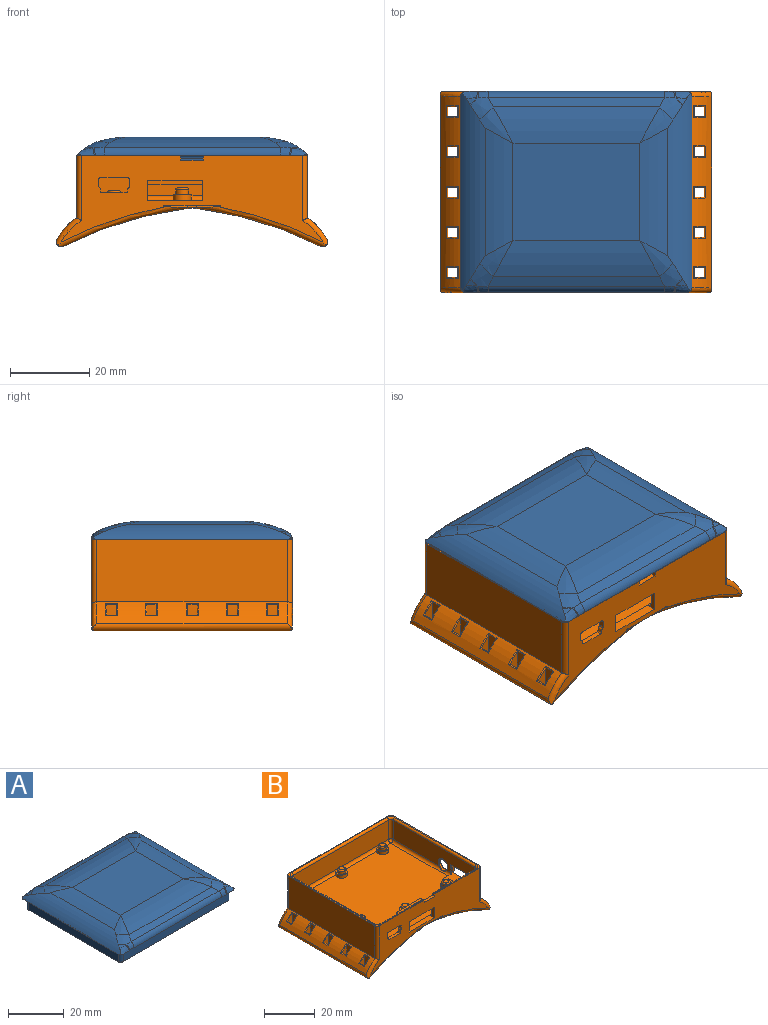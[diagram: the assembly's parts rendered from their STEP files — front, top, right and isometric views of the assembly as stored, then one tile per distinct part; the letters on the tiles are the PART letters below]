
ASSEMBLY  parts=2 mates=1
PART A: 92 faces, bbox 60.7x52.8x9.7 mm
  f0: plane 58.47x50.85mm, normal (0,0,-1), area 85.3mm2, adj f36,f37,f38,f39,f56,f57,f66,f67
  f1: cylinder r=1.27mm len=3.66mm, axis (0,0,1), area 7.3mm2, adj f5,f8,f59,f86
  f2: plane 0.08x0.07mm, normal (0,0,1), area 0mm2, adj f13,f80,f81
  f3: plane 0.08x0.07mm, normal (0,0,1), area 0mm2, adj f15,f80,f82
  f4: plane 0.08x0.07mm, normal (0,0,1), area 0mm2, adj f17,f82,f83
  f5: plane 45.72x3.66mm, normal (1,0,0), area 167.2mm2, adj f1,f9,f61,f84
  f6: plane 53.34x3.66mm, normal (0,1,0), area 195.1mm2, adj f9,f10,f65,f87
  f7: plane 45.72x3.66mm, normal (-1,0,0), area 167.2mm2, adj f10,f11,f62,f91
  f8: plane 53.34x3.66mm, normal (0,-1,0), area 195.1mm2, adj f1,f11,f58,f88
  f9: cylinder r=1.27mm len=3.66mm, axis (0,0,1), area 7.3mm2, adj f5,f6,f63,f85
  f10: cylinder r=1.27mm len=3.66mm, axis (0,0,1), area 7.3mm2, adj f6,f7,f64,f89
  f11: cylinder r=1.27mm len=3.66mm, axis (0,0,1), area 7.3mm2, adj f7,f8,f60,f90
  f12: plane 53.34x4.23mm, normal (0,-1,0), area 225.8mm2, adj f13,f19,f20,f81
  f13: cylinder r=0.64mm len=5.08mm, axis (0,0,1), area 4.7mm2, adj f2,f12,f14,f20,f80,f81
  f14: plane 45.72x4.21mm, normal (-1,0,0), area 192.3mm2, adj f13,f15,f20,f80
  f15: cylinder r=0.64mm len=5.08mm, axis (0,0,1), area 4.7mm2, adj f3,f14,f16,f20,f80,f82
  f16: plane 53.34x4.23mm, normal (0,1,0), area 225.8mm2, adj f15,f17,f20,f82
  f17: cylinder r=0.64mm len=5.08mm, axis (0,0,1), area 4.7mm2, adj f4,f16,f18,f20,f82,f83
  f18: plane 45.72x4.21mm, normal (1,0,0), area 192.3mm2, adj f17,f19,f20,f83
  f19: cylinder r=0.64mm len=5.08mm, axis (0,0,1), area 4.7mm2, adj f12,f18,f20,f21,f81,f83
  f20: plane 54.86x47.24mm, normal (0,0,-1), area 25.7mm2, adj f12,f13,f14,f15,f16,f17,f18,f19
  f21: plane 0.08x0.07mm, normal (0,0,1), area 0mm2, adj f19,f81,f83
  f22: plane 32.07x24.59mm, normal (0,0,1), area 788.5mm2, adj f23,f24,f25,f26
  f23: cylinder r=27.94mm len=42.07mm, axis (-1,0,0), area 346.3mm2, adj f22,f27,f43,f51
  f24: cylinder r=27.94mm len=32.23mm, axis (0,-1,0), area 201.2mm2, adj f22,f47,f51,f56
  f25: cylinder r=27.94mm len=32.23mm, axis (0,1,0), area 201.2mm2, adj f22,f43,f55,f57
  f26: cylinder r=27.94mm len=42.07mm, axis (-1,0,0), area 346.3mm2, adj f22,f28,f47,f55
  f27: cylinder r=25.4mm len=44.62mm, axis (-1,0,0), area 116.8mm2, adj f23,f42,f50,f76
  f28: cylinder r=25.4mm len=44.62mm, axis (-1,0,0), area 116.8mm2, adj f26,f46,f54,f69
  f29: plane 32.07x24.59mm, normal (0,0,-1), area 788.5mm2, adj f30,f31,f32,f33
  f30: cylinder r=26.67mm len=49.57mm, axis (-1,0,0), area 364mm2, adj f29,f31,f32,f34
  f31: cylinder r=26.67mm len=43.88mm, axis (0,-1,0), area 339.2mm2, adj f29,f30,f33,f34,f35,f80,f81,f82
  f32: cylinder r=26.67mm len=43.88mm, axis (0,1,0), area 339.2mm2, adj f29,f30,f33,f34,f35,f81,f82,f83
  f33: cylinder r=26.67mm len=49.57mm, axis (-1,0,0), area 364mm2, adj f29,f31,f32,f35
  f34: cylinder r=24.13mm len=51.24mm, axis (-1,0,0), area 44.6mm2, adj f30,f31,f32,f82
  f35: cylinder r=24.13mm len=51.24mm, axis (-1,0,0), area 44.6mm2, adj f31,f32,f33,f81
  f36: cylinder r=1.27mm len=1.27mm, axis (0,0,-1), area 0.4mm2, adj f0,f57,f70
  f37: cylinder r=1.27mm len=1.27mm, axis (0,0,1), area 0.4mm2, adj f0,f56,f66
  f38: cylinder r=1.27mm len=1.27mm, axis (0,0,1), area 0.4mm2, adj f0,f57,f73
  f39: cylinder r=1.27mm len=1.27mm, axis (0,0,-1), area 0.4mm2, adj f0,f56,f79
  f40: cylinder r=12.7mm len=3.03mm, axis (-0.67,-0.65,-0.36), area 2.4mm2, adj f41,f57,f73
  f41: bspline ~8.74x8.09mm, area 0.7mm2, adj f40,f42,f57,f74
  f42: bspline ~9.46x9.22mm, area 21mm2, adj f27,f41,f43,f57,f75
  f43: bspline ~11.54x11.54mm, area 23.2mm2, adj f23,f25,f42,f57
  f44: cylinder r=12.7mm len=3.03mm, axis (0.67,0.65,-0.36), area 2.4mm2, adj f45,f56,f66
  f45: bspline ~8.74x8.09mm, area 0.7mm2, adj f44,f46,f56,f67
  f46: bspline ~9.46x9.22mm, area 21mm2, adj f28,f45,f47,f56,f68
  f47: bspline ~11.54x11.54mm, area 28.9mm2, adj f24,f26,f46,f56
  f48: cylinder r=12.7mm len=3.03mm, axis (0.67,-0.65,-0.36), area 2.4mm2, adj f49,f56,f79
  f49: bspline ~8.74x8.09mm, area 0.7mm2, adj f48,f50,f56,f78
  f50: bspline ~9.46x9.22mm, area 21mm2, adj f27,f49,f51,f56,f77
  f51: bspline ~11.54x11.54mm, area 29.1mm2, adj f23,f24,f50,f56
  f52: cylinder r=12.7mm len=3.03mm, axis (-0.67,0.65,-0.36), area 2.4mm2, adj f53,f57,f70
  f53: bspline ~8.74x8.09mm, area 0.7mm2, adj f52,f54,f57,f72
  f54: bspline ~9.46x9.22mm, area 21mm2, adj f28,f53,f55,f57,f71
  f55: bspline ~11.54x11.54mm, area 23.1mm2, adj f25,f26,f54,f57
  f56: cylinder r=12.7mm len=50.01mm, axis (0,-1,0), area 307.2mm2, adj f0,f24,f37,f39,f44,f45,f46,f47
  f57: cylinder r=12.7mm len=50.01mm, axis (0,-1,0), area 307.2mm2, adj f0,f25,f36,f38,f40,f41,f42,f43
  f58: plane 53.34x0.51mm, normal (0,-0.71,-0.71), area 38.3mm2, adj f8,f20,f59,f60
  f59: cone r=0.76mm half-angle=45deg, axis (0,0,1), area 1.1mm2, adj f1,f20,f58,f61
  f60: cone r=0.76mm half-angle=45deg, axis (0,0,1), area 1.1mm2, adj f11,f20,f58,f62
  f61: plane 45.72x0.51mm, normal (0.71,0,-0.71), area 32.8mm2, adj f5,f20,f59,f63
  f62: plane 45.72x0.51mm, normal (-0.71,0,-0.71), area 32.8mm2, adj f7,f20,f60,f64
  f63: cone r=0.76mm half-angle=45deg, axis (0,0,1), area 1.1mm2, adj f9,f20,f61,f65
  f64: cone r=0.76mm half-angle=45deg, axis (0,0,1), area 1.1mm2, adj f10,f20,f62,f65
  f65: plane 53.34x0.51mm, normal (0,0.71,-0.71), area 38.3mm2, adj f6,f20,f63,f64
  f66: bspline ~5.85x1.98mm, area 7.9mm2, adj f0,f37,f44,f56,f67
  f67: bspline ~3.43x2.05mm, area 0.8mm2, adj f0,f45,f66,f68
  f68: bspline ~4.23x2.05mm, area 6.3mm2, adj f0,f46,f67,f69
  f69: cylinder r=2.54mm len=44.62mm, axis (-1,0,0), area 116.3mm2, adj f0,f28,f68,f71
  f70: bspline ~5.85x1.98mm, area 7.9mm2, adj f0,f36,f52,f57,f72
  f71: bspline ~4.23x2.05mm, area 6.3mm2, adj f0,f54,f69,f72
  f72: bspline ~3.43x2.05mm, area 0.8mm2, adj f0,f53,f70,f71
  f73: bspline ~5.85x1.98mm, area 7.9mm2, adj f0,f38,f40,f57,f74
  f74: bspline ~3.43x2.05mm, area 0.8mm2, adj f0,f41,f73,f75
  f75: bspline ~4.23x2.05mm, area 6.3mm2, adj f0,f42,f74,f76
  f76: cylinder r=2.54mm len=44.62mm, axis (1,0,0), area 116.3mm2, adj f0,f27,f75,f77
  f77: bspline ~4.23x2.05mm, area 6.3mm2, adj f0,f50,f76,f78
  f78: bspline ~3.43x2.05mm, area 0.8mm2, adj f0,f49,f77,f79
  f79: bspline ~5.85x1.98mm, area 7.9mm2, adj f0,f39,f48,f56,f78
  f80: cylinder r=2.54mm len=46.7mm, axis (0,-1,0), area 139.3mm2, adj f2,f3,f13,f14,f15,f31,f81,f82
  f81: cylinder r=2.54mm len=54.3mm, axis (-1,0,0), area 162.2mm2, adj f2,f12,f13,f19,f21,f31,f32,f35
  f82: cylinder r=2.54mm len=54.3mm, axis (-1,0,0), area 162.2mm2, adj f3,f4,f15,f16,f17,f31,f32,f34
  f83: cylinder r=2.54mm len=46.7mm, axis (0,1,0), area 139.3mm2, adj f4,f17,f18,f19,f21,f32,f81,f82
  f84: cylinder r=0.89mm len=45.72mm, axis (0,-1,0), area 63.8mm2, adj f0,f5,f85,f86
  f85: torus R=2.16mm, axis (0,0,1), area 3.5mm2, adj f0,f9,f84,f87
  f86: torus R=2.16mm, axis (0,0,1), area 3.5mm2, adj f0,f1,f84,f88
  f87: cylinder r=0.89mm len=53.34mm, axis (1,0,0), area 74.5mm2, adj f0,f6,f85,f89
  f88: cylinder r=0.89mm len=53.34mm, axis (-1,0,0), area 74.5mm2, adj f0,f8,f86,f90
  f89: torus R=2.16mm, axis (0,0,1), area 3.5mm2, adj f0,f10,f87,f91
  f90: torus R=2.16mm, axis (0,0,1), area 3.5mm2, adj f0,f11,f88,f91
  f91: cylinder r=0.89mm len=45.72mm, axis (0,1,0), area 63.8mm2, adj f0,f7,f89,f90
PART B: 229 faces, bbox 72x51.8x23.6 mm
  f0: plane 53.34x45.74mm, normal (0,0,1), area 2322.8mm2, adj f4,f6,f9,f19,f20,f24,f148,f149
  f1: plane 58.42x50.8mm, normal (0,0,1), area 83.1mm2, adj f2,f5,f7,f12,f13,f27,f28,f29
  f2: plane 66.13x21.85mm, normal (0,-1,0), area 751.9mm2, adj f1,f11,f27,f30,f34,f35,f81,f82
  f3: plane 53.34x9.27mm, normal (0,1,0), area 401.1mm2, adj f4,f5,f16,f18,f19,f176,f181,f182
  f4: cylinder r=1.27mm len=23.96mm, axis (1,0,0), area 47.8mm2, adj f0,f3,f22,f187
  f5: cylinder r=0.89mm len=23.81mm, axis (-1,0,0), area 33.3mm2, adj f1,f3,f174,f192
  f6: cylinder r=1.27mm len=32.64mm, axis (0,1,0), area 61.6mm2, adj f0,f8,f25,f146,f149,f156,f169
  f7: plane 48.26x15.75mm, normal (1,0,0), area 688mm2, adj f1,f27,f28,f79,f135,f136,f137,f138
  f8: plane 45.72x9.27mm, normal (-1,0,0), area 356.1mm2, adj f6,f9,f18,f26,f155,f158,f159,f160
  f9: cylinder r=1.27mm len=1.27mm, axis (0,1,0), area 1.6mm2, adj f0,f8,f22,f146,f148,f157
  f10: plane 10.45x0.22mm, normal (0,0,-1), area 0.7mm2, adj f12,f31,f32,f33
  f11: plane 14.41x0.75mm, normal (0,0,-1), area 6.1mm2, adj f2,f34,f35,f90,f91,f92,f93,f94
  f12: plane 66.13x21.85mm, normal (0,1,0), area 858.1mm2, adj f1,f10,f28,f29,f31,f32,f87,f89
  f13: plane 48.26x15.75mm, normal (-1,0,0), area 760mm2, adj f1,f29,f30,f78
  f14: plane 53.34x9.27mm, normal (0,-1,0), area 494.5mm2, adj f21,f24,f26,f177
  f15: plane 45.72x9.27mm, normal (1,0,0), area 423.9mm2, adj f16,f20,f21,f180
  f16: cylinder r=1.27mm len=9.27mm, axis (0,0,-1), area 18.5mm2, adj f3,f15,f17,f178
  f17: sphere r=1.27mm, area 2.5mm2, adj f16,f19,f20
  f18: cylinder r=1.27mm len=9.27mm, axis (0,0,1), area 18.5mm2, adj f3,f8,f22,f174
  f19: cylinder r=1.27mm len=15.49mm, axis (1,0,0), area 30.9mm2, adj f0,f3,f17,f188
  f20: cylinder r=1.27mm len=45.72mm, axis (0,-1,0), area 91.2mm2, adj f0,f15,f17,f23
  f21: cylinder r=1.27mm len=9.27mm, axis (0,0,1), area 18.5mm2, adj f14,f15,f23,f179
  f22: sphere r=1.27mm, area 2.5mm2, adj f4,f9,f18
  f23: sphere r=1.27mm, area 3.5mm2, adj f20,f21,f24
  f24: cylinder r=1.27mm len=53.34mm, axis (-1,0,0), area 106.4mm2, adj f0,f14,f23,f25,f217,f224
  f25: sphere r=1.27mm, area 1.6mm2, adj f6,f24,f26
  f26: cylinder r=1.27mm len=9.27mm, axis (0,0,-1), area 18.5mm2, adj f8,f14,f25,f175
  f27: cylinder r=1.27mm len=16.43mm, axis (0,0,-1), area 32.1mm2, adj f1,f2,f7,f88
  f28: cylinder r=1.27mm len=16.43mm, axis (0,0,1), area 32.1mm2, adj f1,f7,f12,f89
  f29: cylinder r=1.27mm len=16.43mm, axis (0,0,-1), area 32.1mm2, adj f1,f12,f13,f87
  f30: cylinder r=1.27mm len=16.43mm, axis (0,0,1), area 32.1mm2, adj f1,f2,f13,f86
  f31: torus R=93.42mm, axis (0,1,0), area 66.3mm2, adj f10,f12,f33,f56,f80,f87
  f32: torus R=93.42mm, axis (0,1,0), area 66.3mm2, adj f10,f12,f33,f57,f83,f89
  f33: bspline ~3.09x1.47mm, area 3.4mm2, adj f10,f31,f32,f85
  f34: cylinder r=0.25mm len=0.25mm, axis (0,0,1), area 0.1mm2, adj f2,f11,f90
  f35: cylinder r=0.25mm len=0.25mm, axis (0,0,-1), area 0.1mm2, adj f2,f11,f94
  f36: plane 5.35x2.65mm, normal (1,0,0), area 13.6mm2, adj f37,f39,f57,f120,f121,f122
  f37: plane 6.4x2.64mm, normal (0,-1,0), area 11.7mm2, adj f36,f38,f57,f119,f121
  f38: plane 3.59x2.54mm, normal (-1,0,0), area 9.1mm2, adj f37,f39,f57,f119
  f39: plane 6.4x2.64mm, normal (0,1,0), area 11.7mm2, adj f36,f38,f57,f119,f120
  f40: plane 6.4x2.64mm, normal (0,1,0), area 11.7mm2, adj f41,f43,f57,f124,f126
  f41: plane 5.35x2.65mm, normal (1,0,0), area 13.6mm2, adj f40,f42,f57,f123,f125,f126
  f42: plane 6.4x2.64mm, normal (0,-1,0), area 11.7mm2, adj f41,f43,f57,f123,f124
  f43: plane 3.59x2.54mm, normal (-1,0,0), area 9.1mm2, adj f40,f42,f57,f124
  f44: plane 6.4x2.64mm, normal (0,1,0), area 11.7mm2, adj f45,f47,f57,f128,f130
  f45: plane 5.35x2.65mm, normal (1,0,0), area 13.6mm2, adj f44,f46,f57,f127,f129,f130
  f46: plane 6.4x2.64mm, normal (0,-1,0), area 11.7mm2, adj f45,f47,f57,f127,f128
  f47: plane 3.59x2.54mm, normal (-1,0,0), area 9.1mm2, adj f44,f46,f57,f128
  f48: plane 6.4x2.64mm, normal (0,1,0), area 11.7mm2, adj f49,f51,f57,f132,f134
  f49: plane 5.35x2.65mm, normal (1,0,0), area 13.6mm2, adj f48,f50,f57,f131,f133,f134
  f50: plane 6.4x2.64mm, normal (0,-1,0), area 11.7mm2, adj f49,f51,f57,f131,f132
  f51: plane 3.59x2.54mm, normal (-1,0,0), area 9.1mm2, adj f48,f50,f57,f132
  f52: plane 6.4x2.64mm, normal (0,1,0), area 11.7mm2, adj f53,f55,f57,f101,f102
  f53: plane 5.35x2.65mm, normal (1,0,0), area 13.6mm2, adj f52,f54,f57,f99,f100,f101
  f54: plane 6.4x2.64mm, normal (0,-1,0), area 11.7mm2, adj f53,f55,f57,f100,f102
  f55: plane 3.59x2.54mm, normal (-1,0,0), area 9.1mm2, adj f52,f54,f57,f102
  f56: cylinder r=92.15mm len=48.26mm, axis (0,-1,0), area 1534.4mm2, adj f31,f58,f59,f60,f61,f62,f63,f64
  f57: cylinder r=92.15mm len=48.26mm, axis (0,-1,0), area 1534.4mm2, adj f32,f36,f37,f38,f39,f40,f41,f42
  f58: plane 5.35x2.65mm, normal (-1,0,0), area 13.6mm2, adj f56,f59,f61,f104,f105,f106
  f59: plane 6.4x2.64mm, normal (0,1,0), area 11.7mm2, adj f56,f58,f60,f103,f105
  f60: plane 3.59x2.54mm, normal (1,0,0), area 9.1mm2, adj f56,f59,f61,f103
  f61: plane 6.4x2.64mm, normal (0,-1,0), area 11.7mm2, adj f56,f58,f60,f103,f104
  f62: plane 6.4x2.64mm, normal (0,1,0), area 11.7mm2, adj f56,f63,f65,f109,f110
  f63: plane 3.59x2.54mm, normal (1,0,0), area 9.1mm2, adj f56,f62,f64,f109
  f64: plane 6.4x2.64mm, normal (0,-1,0), area 11.7mm2, adj f56,f63,f65,f107,f109
  f65: plane 5.35x2.65mm, normal (-1,0,0), area 13.6mm2, adj f56,f62,f64,f107,f108,f110
  f66: plane 6.4x2.64mm, normal (0,1,0), area 11.7mm2, adj f56,f67,f69,f113,f114
  f67: plane 3.59x2.54mm, normal (1,0,0), area 9.1mm2, adj f56,f66,f68,f113
  f68: plane 6.4x2.64mm, normal (0,-1,0), area 11.7mm2, adj f56,f67,f69,f111,f113
  f69: plane 5.35x2.65mm, normal (-1,0,0), area 13.6mm2, adj f56,f66,f68,f111,f112,f114
  f70: plane 6.4x2.64mm, normal (0,1,0), area 11.7mm2, adj f56,f71,f73,f117,f118
  f71: plane 3.59x2.54mm, normal (1,0,0), area 9.1mm2, adj f56,f70,f72,f117
  f72: plane 6.4x2.64mm, normal (0,-1,0), area 11.7mm2, adj f56,f71,f73,f115,f117
  f73: plane 5.35x2.65mm, normal (-1,0,0), area 13.6mm2, adj f56,f70,f72,f115,f116,f118
  f74: plane 6.4x2.64mm, normal (0,1,0), area 11.7mm2, adj f56,f75,f77,f95,f97
  f75: plane 3.59x2.54mm, normal (1,0,0), area 9.1mm2, adj f56,f74,f76,f95
  f76: plane 6.4x2.64mm, normal (0,-1,0), area 11.7mm2, adj f56,f75,f77,f95,f96
  f77: plane 5.35x2.65mm, normal (-1,0,0), area 13.6mm2, adj f56,f74,f76,f96,f97,f98
  f78: cylinder r=15.97mm len=48.26mm, axis (0,-1,0), area 294.2mm2, adj f13,f80,f86,f87,f95,f96,f97,f98
  f79: cylinder r=15.97mm len=48.26mm, axis (0,-1,0), area 294.2mm2, adj f7,f83,f88,f89,f99,f100,f101,f102
  f80: cylinder r=1.27mm len=50.68mm, axis (0,1,0), area 160mm2, adj f31,f56,f78,f81,f86,f87
  f81: torus R=93.42mm, axis (0,-1,0), area 63.9mm2, adj f2,f56,f80,f84,f86,f91
  f82: torus R=93.42mm, axis (0,-1,0), area 63.9mm2, adj f2,f57,f83,f84,f88,f93
  f83: cylinder r=1.27mm len=50.68mm, axis (0,1,0), area 160mm2, adj f32,f57,f79,f82,f88,f89
  f84: bspline ~3.09x1.1mm, area 2.3mm2, adj f81,f82,f85,f92
  f85: cylinder r=12.7mm len=48.26mm, axis (0,1,0), area 149.4mm2, adj f33,f56,f57,f84
  f86: torus R=14.7mm, axis (0,-1,0), area 16.4mm2, adj f2,f30,f78,f80,f81
  f87: torus R=14.7mm, axis (0,1,0), area 16.4mm2, adj f12,f29,f31,f78,f80
  f88: torus R=14.7mm, axis (0,-1,0), area 16.4mm2, adj f2,f27,f79,f82,f83
  f89: torus R=14.7mm, axis (0,1,0), area 16.4mm2, adj f12,f28,f32,f79,f83
  f90: cylinder r=0.25mm len=0.47mm, axis (1,0,0), area 0.1mm2, adj f2,f11,f34,f91
  f91: bspline ~7.56x0.86mm, area 2.8mm2, adj f11,f81,f90,f92
  f92: bspline ~3.38x0.87mm, area 1.5mm2, adj f11,f84,f91,f93
  f93: bspline ~7.56x0.86mm, area 2.8mm2, adj f11,f82,f92,f94
  f94: cylinder r=0.25mm len=0.54mm, axis (1,0,0), area 0.2mm2, adj f2,f11,f35,f93
  f95: cylinder r=0.25mm len=3.05mm, axis (0,-1,0), area 1.7mm2, adj f74,f75,f76,f78,f96,f97
  f96: torus R=15.72mm, axis (0,-1,0), area 1.6mm2, adj f76,f77,f78,f95,f98
  f97: torus R=15.72mm, axis (0,1,0), area 1.6mm2, adj f74,f77,f78,f95,f98
  f98: cylinder r=0.25mm len=3.05mm, axis (0,-1,0), area 0.7mm2, adj f77,f78,f96,f97
  f99: cylinder r=0.25mm len=3.05mm, axis (0,-1,0), area 0.7mm2, adj f53,f79,f100,f101
  f100: torus R=15.72mm, axis (0,1,0), area 1.6mm2, adj f53,f54,f79,f99,f102
  f101: torus R=15.72mm, axis (0,-1,0), area 1.6mm2, adj f52,f53,f79,f99,f102
  f102: cylinder r=0.25mm len=3.05mm, axis (0,-1,0), area 1.7mm2, adj f52,f54,f55,f79,f100,f101
  f103: cylinder r=0.25mm len=3.05mm, axis (0,-1,0), area 1.7mm2, adj f59,f60,f61,f78,f104,f105
  f104: torus R=15.72mm, axis (0,-1,0), area 1.6mm2, adj f58,f61,f78,f103,f106
  f105: torus R=15.72mm, axis (0,1,0), area 1.6mm2, adj f58,f59,f78,f103,f106
  f106: cylinder r=0.25mm len=3.05mm, axis (0,-1,0), area 0.7mm2, adj f58,f78,f104,f105
  f107: torus R=15.72mm, axis (0,-1,0), area 1.6mm2, adj f64,f65,f78,f108,f109
  f108: cylinder r=0.25mm len=3.05mm, axis (0,-1,0), area 0.7mm2, adj f65,f78,f107,f110
  f109: cylinder r=0.25mm len=3.05mm, axis (0,-1,0), area 1.7mm2, adj f62,f63,f64,f78,f107,f110
  f110: torus R=15.72mm, axis (0,1,0), area 1.6mm2, adj f62,f65,f78,f108,f109
  f111: torus R=15.72mm, axis (0,-1,0), area 1.6mm2, adj f68,f69,f78,f112,f113
  f112: cylinder r=0.25mm len=3.05mm, axis (0,-1,0), area 0.7mm2, adj f69,f78,f111,f114
  f113: cylinder r=0.25mm len=3.05mm, axis (0,-1,0), area 1.7mm2, adj f66,f67,f68,f78,f111,f114
  f114: torus R=15.72mm, axis (0,1,0), area 1.6mm2, adj f66,f69,f78,f112,f113
  f115: torus R=15.72mm, axis (0,-1,0), area 1.6mm2, adj f72,f73,f78,f116,f117
  f116: cylinder r=0.25mm len=3.05mm, axis (0,-1,0), area 0.7mm2, adj f73,f78,f115,f118
  f117: cylinder r=0.25mm len=3.05mm, axis (0,-1,0), area 1.7mm2, adj f70,f71,f72,f78,f115,f118
  f118: torus R=15.72mm, axis (0,1,0), area 1.6mm2, adj f70,f73,f78,f116,f117
  f119: cylinder r=0.25mm len=3.05mm, axis (0,-1,0), area 1.7mm2, adj f37,f38,f39,f79,f120,f121
  f120: torus R=15.72mm, axis (0,-1,0), area 1.6mm2, adj f36,f39,f79,f119,f122
  f121: torus R=15.72mm, axis (0,1,0), area 1.6mm2, adj f36,f37,f79,f119,f122
  f122: cylinder r=0.25mm len=3.05mm, axis (0,-1,0), area 0.7mm2, adj f36,f79,f120,f121
  f123: torus R=15.72mm, axis (0,1,0), area 1.6mm2, adj f41,f42,f79,f124,f125
  f124: cylinder r=0.25mm len=3.05mm, axis (0,-1,0), area 1.7mm2, adj f40,f42,f43,f79,f123,f126
  f125: cylinder r=0.25mm len=3.05mm, axis (0,-1,0), area 0.7mm2, adj f41,f79,f123,f126
  f126: torus R=15.72mm, axis (0,-1,0), area 1.6mm2, adj f40,f41,f79,f124,f125
  f127: torus R=15.72mm, axis (0,1,0), area 1.6mm2, adj f45,f46,f79,f128,f129
  f128: cylinder r=0.25mm len=3.05mm, axis (0,-1,0), area 1.7mm2, adj f44,f46,f47,f79,f127,f130
  f129: cylinder r=0.25mm len=3.05mm, axis (0,-1,0), area 0.7mm2, adj f45,f79,f127,f130
  f130: torus R=15.72mm, axis (0,-1,0), area 1.6mm2, adj f44,f45,f79,f128,f129
  f131: torus R=15.72mm, axis (0,1,0), area 1.6mm2, adj f49,f50,f79,f132,f133
  f132: cylinder r=0.25mm len=3.05mm, axis (0,-1,0), area 1.7mm2, adj f48,f50,f51,f79,f131,f134
  f133: cylinder r=0.25mm len=3.05mm, axis (0,-1,0), area 0.7mm2, adj f49,f79,f131,f134
  f134: torus R=15.72mm, axis (0,-1,0), area 1.6mm2, adj f48,f49,f79,f132,f133
  f135: plane 1.02x0.38mm, normal (0,0,-1), area 0.4mm2, adj f7,f136,f144,f167
  f136: plane 1.91x1.02mm, normal (0,-1,0), area 1.9mm2, adj f7,f135,f137,f166
  f137: plane 1.02x0.38mm, normal (0,0,1), area 0.4mm2, adj f7,f136,f138,f165
  f138: plane 1.1x1.02mm, normal (0,-1,0), area 1.1mm2, adj f7,f137,f139,f164
  f139: plane 12.2x1.02mm, normal (0,0,-1), area 12.4mm2, adj f7,f138,f140,f163
  f140: plane 1.1x1.02mm, normal (0,1,0), area 1.1mm2, adj f7,f139,f141,f162
  f141: plane 1.02x0.38mm, normal (0,0,1), area 0.4mm2, adj f7,f140,f142,f161
  f142: plane 1.91x1.02mm, normal (0,1,0), area 1.9mm2, adj f7,f141,f143,f160
  f143: plane 1.02x0.38mm, normal (0,0,-1), area 0.4mm2, adj f7,f142,f145,f159
  f144: plane 1.1x1.1mm, normal (0,-1,0), area 1.1mm2, adj f7,f135,f146,f168,f169
  f145: plane 1.1x1.1mm, normal (0,1,0), area 1.1mm2, adj f7,f143,f146,f157,f158
  f146: plane 12.74x6.38mm, normal (0,0,1), area 69.8mm2, adj f6,f7,f9,f144,f145,f148,f149,f150
  f147: cylinder r=2.48mm len=4.95mm, axis (1,0,0), area 13.2mm2, adj f155,f156,f170
  f148: plane 4.98x0.78mm, normal (0,-1,0), area 3.6mm2, adj f0,f9,f146,f150
  f149: plane 4.98x0.78mm, normal (0,1,0), area 3.6mm2, adj f0,f6,f146,f150
  f150: plane 12.2x1.8mm, normal (-1,0,0), area 17.3mm2, adj f0,f146,f148,f149,f151,f152,f154
  f151: plane 1.02x1.02mm, normal (0,1,0), area 1mm2, adj f146,f150,f153,f154
  f152: plane 1.02x1.02mm, normal (0,-1,0), area 1mm2, adj f146,f150,f153,f154
  f153: plane 7.62x1.02mm, normal (1,0,0), area 7.7mm2, adj f146,f151,f152,f154
  f154: plane 7.62x1.02mm, normal (0,0,1), area 7.7mm2, adj f150,f151,f152,f153
  f155: torus R=2.73mm, axis (1,0,0), area 4.5mm2, adj f8,f147,f156
  f156: bspline ~4.71x1.39mm, area 1.3mm2, adj f6,f147,f155
  f157: torus R=1.52mm, axis (0,-1,0), area 0.2mm2, adj f9,f145,f146,f158
  f158: cylinder r=0.25mm len=0.86mm, axis (0,0,-1), area 0.3mm2, adj f8,f145,f157,f159
  f159: cylinder r=0.25mm len=0.64mm, axis (0,-1,0), area 0.2mm2, adj f8,f143,f158,f160
  f160: cylinder r=0.25mm len=1.91mm, axis (0,0,-1), area 0.7mm2, adj f8,f142,f159,f161
  f161: cylinder r=0.25mm len=0.64mm, axis (0,1,0), area 0.2mm2, adj f8,f141,f160,f162
  f162: cylinder r=0.25mm len=1.61mm, axis (0,0,-1), area 0.5mm2, adj f8,f140,f161,f163
  f163: cylinder r=0.25mm len=12.71mm, axis (0,-1,0), area 5mm2, adj f8,f139,f162,f164
  f164: cylinder r=0.25mm len=1.61mm, axis (0,0,1), area 0.5mm2, adj f8,f138,f163,f165
  f165: cylinder r=0.25mm len=0.64mm, axis (0,1,0), area 0.2mm2, adj f8,f137,f164,f166
  f166: cylinder r=0.25mm len=1.91mm, axis (0,0,1), area 0.7mm2, adj f8,f136,f165,f167
  f167: cylinder r=0.25mm len=0.64mm, axis (0,-1,0), area 0.2mm2, adj f8,f135,f166,f168
  f168: cylinder r=0.25mm len=0.86mm, axis (0,0,1), area 0.3mm2, adj f8,f144,f167,f169
  f169: torus R=1.52mm, axis (0,-1,0), area 0.2mm2, adj f6,f144,f146,f168
  f170: torus R=2.73mm, axis (1,0,0), area 6.4mm2, adj f7,f147
  f171: cylinder r=1.62mm len=3.25mm, axis (0,0,-1), area 20.8mm2, adj f0,f206
  f172: plane 2.25x2.25mm, normal (0,0,1), area 4mm2, adj f206
  f173: cylinder r=0.89mm len=45.72mm, axis (0,-1,0), area 63.8mm2, adj f1,f8,f174,f175
  f174: torus R=2.16mm, axis (0,0,1), area 3.5mm2, adj f1,f5,f18,f173
  f175: torus R=2.16mm, axis (0,0,1), area 3.5mm2, adj f1,f26,f173,f177
  f176: cylinder r=0.89mm len=23.81mm, axis (-1,0,0), area 33.3mm2, adj f1,f3,f178,f193
  f177: cylinder r=0.89mm len=53.34mm, axis (1,0,0), area 74.5mm2, adj f1,f14,f175,f179
  f178: torus R=2.16mm, axis (0,0,1), area 3.5mm2, adj f1,f16,f176,f180
  f179: torus R=2.16mm, axis (0,0,1), area 3.5mm2, adj f1,f21,f177,f180
  f180: cylinder r=0.89mm len=45.72mm, axis (0,1,0), area 63.8mm2, adj f1,f15,f178,f179
  f181: plane 13.89x6.22mm, normal (0,0,1), area 86.5mm2, adj f3,f182,f184,f185
  f182: plane 6.22x1.78mm, normal (1,0,0), area 5.6mm2, adj f3,f181,f183,f185,f189,f190
  f183: plane 13.9x0.89mm, normal (0,0,-1), area 12.4mm2, adj f182,f184,f185,f190
  f184: plane 6.22x1.78mm, normal (-1,0,0), area 5.6mm2, adj f3,f181,f183,f185,f189,f190
  f185: plane 13.89x1.78mm, normal (0,1,0), area 24.7mm2, adj f181,f182,f183,f184
  f186: plane 13.9x2.54mm, normal (0,0,1), area 35.2mm2, adj f0,f2,f187,f188
  f187: plane 5x2.54mm, normal (-1,0,0), area 6.7mm2, adj f2,f3,f4,f186,f189
  f188: plane 5x2.54mm, normal (1,0,0), area 6.7mm2, adj f2,f3,f19,f186,f189
  f189: plane 13.9x6.6mm, normal (0,0,-1), area 91.8mm2, adj f2,f182,f184,f187,f188,f190
  f190: plane 13.9x1.02mm, normal (0,-1,0), area 14.1mm2, adj f182,f183,f184,f189
  f191: plane 5.72x1.27mm, normal (0,0,1), area 7.3mm2, adj f2,f3,f192,f193
  f192: plane 1.27x1.23mm, normal (-1,0,0), area 1.4mm2, adj f1,f2,f3,f5,f191
  f193: plane 1.27x1.23mm, normal (1,0,0), area 1.4mm2, adj f1,f2,f3,f176,f191
  f194: extruded ~1.27x1.06mm, area 1.5mm2, adj f2,f3,f200,f205
  f195: plane 6.04x1.27mm, normal (0,0,1), area 7.7mm2, adj f2,f3,f204,f205
  f196: extruded ~1.27x1.06mm, area 1.5mm2, adj f2,f3,f203,f204
  f197: plane 1.33x1.27mm, normal (1,0,0), area 1.7mm2, adj f2,f3,f202,f203
  f198: plane 6.73x1.27mm, normal (0,0,-1), area 8.5mm2, adj f2,f3,f201,f202
  f199: plane 1.33x1.27mm, normal (-1,0,0), area 1.7mm2, adj f2,f3,f200,f201
  f200: cylinder r=0.64mm len=1.27mm, axis (0,1,0), area 0.7mm2, adj f2,f3,f194,f199
  f201: cylinder r=0.64mm len=1.27mm, axis (0,1,0), area 1.3mm2, adj f2,f3,f198,f199
  f202: cylinder r=0.64mm len=1.27mm, axis (0,-1,0), area 1.3mm2, adj f2,f3,f197,f198
  f203: cylinder r=0.64mm len=1.27mm, axis (0,1,0), area 0.7mm2, adj f2,f3,f196,f197
  f204: cylinder r=0.38mm len=1.27mm, axis (0,1,0), area 0.7mm2, adj f2,f3,f195,f196
  f205: cylinder r=0.38mm len=1.27mm, axis (0,1,0), area 0.7mm2, adj f2,f3,f194,f195
  f206: torus R=1.12mm, axis (0,0,1), area 7.1mm2, adj f171,f172
  f207: cylinder r=2.25mm len=4.5mm, axis (0,0,-1), area 21.2mm2, adj f0,f208
  f208: plane 4.5x4.5mm, normal (0,0,1), area 7.6mm2, adj f207,f211
  f209: plane 2.25x2.25mm, normal (0,0,1), area 4mm2, adj f210
  f210: torus R=1.13mm, axis (0,0,1), area 7.1mm2, adj f209,f211
  f211: cylinder r=1.63mm len=3.25mm, axis (0,0,-1), area 12.8mm2, adj f208,f210
  f212: cylinder r=2.25mm len=4.5mm, axis (0,0,-1), area 21.2mm2, adj f0,f213
  f213: plane 4.5x4.5mm, normal (0,0,1), area 7.6mm2, adj f212,f216
  f214: plane 2.25x2.25mm, normal (0,0,1), area 4mm2, adj f215
  f215: torus R=1.13mm, axis (0,0,1), area 7.1mm2, adj f214,f216
  f216: cylinder r=1.63mm len=3.25mm, axis (0,0,-1), area 12.8mm2, adj f213,f215
  f217: plane 3.06x1.5mm, normal (0,1,0), area 4.6mm2, adj f24,f218,f219
  f218: cylinder r=2.25mm len=4.5mm, axis (0,0,-1), area 16.2mm2, adj f0,f217,f219
  f219: plane 4.5x3.9mm, normal (0,0,1), area 6.3mm2, adj f217,f218,f222
  f220: plane 2.25x2.25mm, normal (0,0,1), area 4mm2, adj f221
  f221: torus R=1.13mm, axis (0,0,1), area 7.1mm2, adj f220,f222
  f222: cylinder r=1.63mm len=3.25mm, axis (0,0,-1), area 12.8mm2, adj f219,f221
  f223: cylinder r=2.25mm len=4.5mm, axis (0,0,-1), area 16.2mm2, adj f0,f224,f225
  f224: plane 3.06x1.5mm, normal (0,1,0), area 4.6mm2, adj f24,f223,f225
  f225: plane 4.5x3.9mm, normal (0,0,1), area 6.3mm2, adj f223,f224,f228
  f226: plane 2.25x2.25mm, normal (0,0,1), area 4mm2, adj f227
  f227: torus R=1.13mm, axis (0,0,1), area 7.1mm2, adj f226,f228
  f228: cylinder r=1.63mm len=3.25mm, axis (0,0,-1), area 12.8mm2, adj f225,f227
PLACE A rot(axis=(-0.13,-0.99,0.01),0deg) t=(7.88,-35.92,-25.51)mm
PLACE B rot(axis=(-0.13,-0.99,0.01),0deg) t=(7.77,-35.94,-25.62)mm
MATE slider A.f29 <-> B.f0  axis (0,0,-1) through (7.88,-35.92,-11.54)mm
